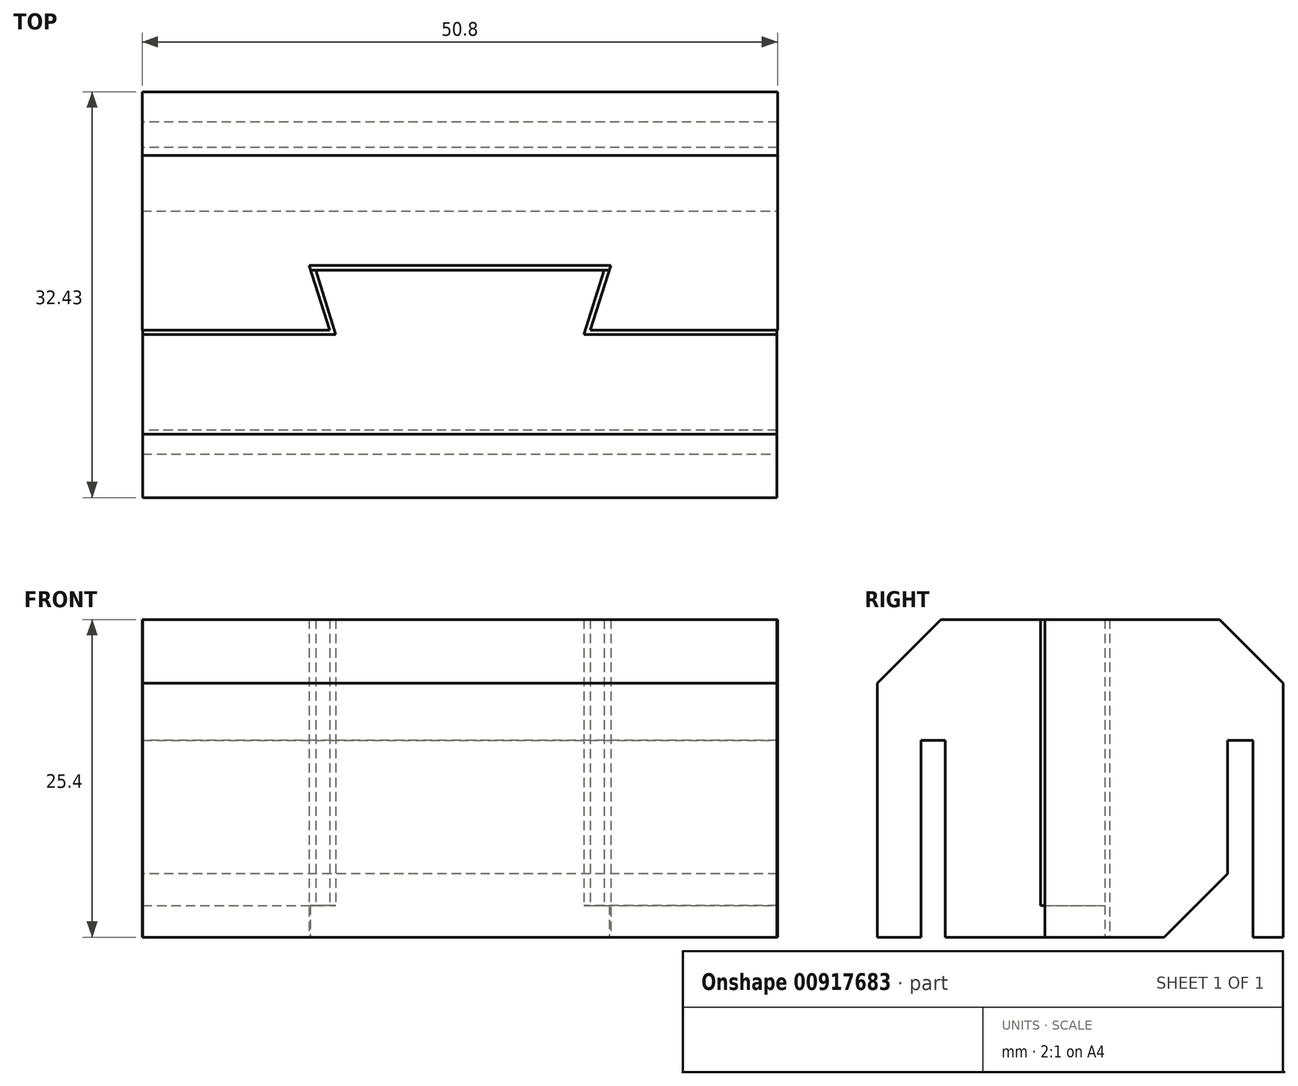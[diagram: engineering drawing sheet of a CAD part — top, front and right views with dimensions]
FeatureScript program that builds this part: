
annotation { "Feature Type Name" : "Feature", "Feature Type Description" : "" }
export const myFeature = defineFeature(function(context is Context, id is Id, definition is map)
    precondition{}
    {
        {
            var Q0;
            Q0=qCreatedBy(makeId("Top.planeOp"),FACE);
            var sketch = newSketch(context, id + "F0", { "sketchPlane" : qUnion([Q0])});
            skLineSegment(sketch, "E0.bottom", {"start": v(25.4, 9.52) * mm, "end": v(-25.4, 9.53) * mm});
            skLineSegment(sketch, "E0.top", {"start": v(25.4, -9.53) * mm, "end": v(10.41, -9.53) * mm});
            skLineSegment(sketch, "E0.left", {"start": v(25.4, 9.52) * mm, "end": v(25.4, -9.53) * mm});
            skLineSegment(sketch, "E0.right", {"start": v(-25.4, 9.53) * mm, "end": v(-25.4, -9.52) * mm});
            skPoint(sketch, "E0.middle", {"position": v(0, 0) * mm});
            skLineSegment(sketch, "E1.bottom", {"start": v(-12.07, -9.53) * mm, "end": v(-10.41, -9.53) * mm});
            skLineSegment(sketch, "E1.top", {"start": v(-12.06, -4.35) * mm, "end": v(12.07, -4.35) * mm});
            skPoint(sketch, "E1.middle", {"position": v(0, -6.94) * mm});
            skLineSegment(sketch, "E2", {"start": v(-12.06, -4.35) * mm, "end": v(-10.41, -9.53) * mm});
            skLineSegment(sketch, "E3.MirrorCS", {"start": v(12.06, -4.35) * mm, "end": v(10.41, -9.52) * mm});
            skLineSegment(sketch, "E4.trimOffspring", {"start": v(-10.41, -9.53) * mm, "end": v(-25.4, -9.53) * mm});
            skLineSegment(sketch, "E5.trimOffspring", {"start": v(10.41, -9.53) * mm, "end": v(12.06, -9.53) * mm});
            skLineSegment(sketch, "E6", {"start": v(-10.41, -9.53) * mm, "end": v(10.41, -9.53) * mm});
            skSolve(sketch);
        }
        {
            var Q0;
            Q0=makeQuery(id+"F0.imprint","IMPRINT",FACE,{"disambiguationData":[TD([[makeQuery(id+"F0.imprint","IMPRINT",EDGE,{"derivedFrom":sQuery(id+"F0.wireOp",EDGE,"E0.bottom")}),1.0]])]});
            extrude(context, id + "F1", {"entities" : qUnion([Q0]), "depth" : 25.4 * mm, "offsetDistance" : 25.4 * mm});
        }
        {
            var Q0;
            Q0=makeQuery(id+"F1.opExtrude","SWEPT_FACE",FACE,{"disambiguationData":[OSD([sQuery(id+"F0.wireOp",EDGE,"E0.right")])]});
            var sketch = newSketch(context, id + "F2", { "sketchPlane" : qUnion([Q0])});
            skLineSegment(sketch, "E7.bottom", {"start": v(-7.13, 0) * mm, "end": v(-5.1, 0) * mm});
            skLineSegment(sketch, "E7.top", {"start": v(-7.13, 15.75) * mm, "end": v(-5.1, 15.75) * mm});
            skLineSegment(sketch, "E7.left", {"start": v(-7.13, 0) * mm, "end": v(-7.13, 15.75) * mm});
            skLineSegment(sketch, "E7.right", {"start": v(-5.1, 0) * mm, "end": v(-5.1, 15.75) * mm});
            skSolve(sketch);
        }
        {
            var Q0;
            Q0=makeQuery(id+"F2.imprint","IMPRINT",FACE,{"disambiguationData":[TD([[makeQuery(id+"F2.imprint","IMPRINT",EDGE,{"derivedFrom":sQuery(id+"F2.wireOp",EDGE,"E7.bottom")}),1.0]])]});
            extrude(context, id + "F3", {"entities" : qUnion([Q0]), "operationType" : NewBodyOperationType.REMOVE, "oppositeDirection" : true, "depth" : 68.33 * mm, "offsetDistance" : 25.4 * mm});
        }
        {
            var Q0;
            Q0=makeQuery(id+"F3.boolean.opBoolean","COPY",EDGE,{"derivedFrom":makeQuery(id+"F3.opExtrude","SWEPT_EDGE",EDGE,{"disambiguationData":[OSD([sQuery(id+"F0.wireOp",EDGE,"E0.right"),sQuery(id+"F2.wireOp",EDGE,"E7.bottom"),sQuery(id+"F2.wireOp",EDGE,"E7.right")])]})});
            var Q1;
            Q1=makeQuery(id+"F1.opExtrude","CAP_EDGE",EDGE,{"disambiguationData":[OSD([sQuery(id+"F0.wireOp",EDGE,"E0.bottom")])],"isStart":false});
            chamfer(context, id + "F4", {"entities" : qUnion([Q0, Q1]), "width" : 5.08 * mm, "tangentPropagation" : true});
        }
        {
            var Q0;
            Q0=qCreatedBy(makeId("Top.planeOp"),FACE);
            var sketch = newSketch(context, id + "F5", { "sketchPlane" : qUnion([Q0])});
            skLineSegment(sketch, "E8", {"start": v(-25.36, -9.86) * mm, "end": v(-9.93, -9.86) * mm});
            skLineSegment(sketch, "E9", {"start": v(-9.93, -9.86) * mm, "end": v(-11.53, -4.72) * mm});
            skLineSegment(sketch, "E10", {"start": v(-11.53, -4.72) * mm, "end": v(0, -4.72) * mm});
            skLineSegment(sketch, "E11", {"start": v(-25.36, -9.86) * mm, "end": v(-25.36, -22.9) * mm});
            skLineSegment(sketch, "E12", {"start": v(-25.36, -22.9) * mm, "end": v(0, -22.9) * mm});
            skLineSegment(sketch, "E13.MirrorCS", {"start": v(25.36, -22.9) * mm, "end": v(0, -22.9) * mm});
            skLineSegment(sketch, "E14.MirrorCS", {"start": v(25.36, -9.86) * mm, "end": v(25.36, -22.9) * mm});
            skLineSegment(sketch, "E15.MirrorCS", {"start": v(25.36, -9.86) * mm, "end": v(9.93, -9.86) * mm});
            skLineSegment(sketch, "E16.MirrorCS", {"start": v(9.93, -9.86) * mm, "end": v(11.53, -4.72) * mm});
            skLineSegment(sketch, "E17.MirrorCS", {"start": v(11.53, -4.72) * mm, "end": v(0, -4.72) * mm});
            skSolve(sketch);
        }
        {
            var Q0;
            Q0=makeQuery(id+"F5.imprint","IMPRINT",FACE,{"disambiguationData":[TD([[makeQuery(id+"F5.imprint","IMPRINT",EDGE,{"derivedFrom":sQuery(id+"F5.wireOp",EDGE,"E8")}),-1.0]])]});
            extrude(context, id + "F6", {"entities" : qUnion([Q0]), "operationType" : NewBodyOperationType.ADD, "depth" : 25.4 * mm, "offsetDistance" : 25.4 * mm});
        }
        {
            var Q0;
            Q0=makeQuery(id+"F6.opExtrude","CAP_FACE",FACE,{"disambiguationData":[OSD([sQuery(id+"F5.wireOp",EDGE,"E8"),sQuery(id+"F5.wireOp",EDGE,"E9"),sQuery(id+"F5.wireOp",EDGE,"E10"),sQuery(id+"F5.wireOp",EDGE,"E11"),sQuery(id+"F5.wireOp",EDGE,"E12"),sQuery(id+"F5.wireOp",EDGE,"E13.MirrorCS"),sQuery(id+"F5.wireOp",EDGE,"E14.MirrorCS"),sQuery(id+"F5.wireOp",EDGE,"E15.MirrorCS"),sQuery(id+"F5.wireOp",EDGE,"E16.MirrorCS"),sQuery(id+"F5.wireOp",EDGE,"E17.MirrorCS")])],"isStart":true});
            var sketch = newSketch(context, id + "F7", { "sketchPlane" : qUnion([Q0])});
            skLineSegment(sketch, "E18", {"start": v(-25.36, 19.4) * mm, "end": v(25.36, 19.4) * mm});
            skLineSegment(sketch, "E19", {"start": v(25.36, 19.4) * mm, "end": v(25.36, 17.5) * mm});
            skLineSegment(sketch, "E20", {"start": v(25.36, 17.5) * mm, "end": v(-25.36, 17.5) * mm});
            skSolve(sketch);
        }
        {
            var Q0;
            {var subQ0=sQuery(id+"F7.wireOp",EDGE,"E18");Q0=makeQuery(id+"F7.imprint","IMPRINT",FACE,{"disambiguationData":[TD([[makeQuery(id+"F7.imprint","IMPRINT",EDGE,{"derivedFrom":subQ0}),-1.0]])]});}
            extrude(context, id + "F8", {"entities" : qUnion([Q0]), "operationType" : NewBodyOperationType.REMOVE, "oppositeDirection" : true, "depth" : 15.75 * mm, "offsetDistance" : 25.4 * mm});
        }
        {
            var Q0;
            {var subQ0=sQuery(id+"F5.wireOp",EDGE,"E17.MirrorCS");var subQ1=sQuery(id+"F5.wireOp",EDGE,"E10");var subQ2=sQuery(id+"F5.wireOp",EDGE,"E9");var subQ3=sQuery(id+"F5.wireOp",EDGE,"E11");var subQ4=sQuery(id+"F5.wireOp",EDGE,"E8");var subQ5=sQuery(id+"F5.wireOp",EDGE,"E14.MirrorCS");var subQ6=sQuery(id+"F5.wireOp",EDGE,"E15.MirrorCS");var subQ7=sQuery(id+"F5.wireOp",EDGE,"E16.MirrorCS");Q0=makeQuery(id+"F8.boolean.opBoolean","SPLIT",FACE,{"disambiguationData":[TD([makeQuery(id+"F6.opExtrude","SWEPT_FACE",FACE,{"disambiguationData":[OSD([subQ4])]})])],"derivedFrom":makeQuery(id+"F6.opExtrude","CAP_FACE",FACE,{"disambiguationData":[OSD([subQ4,subQ2,subQ1,subQ3,sQuery(id+"F5.wireOp",EDGE,"E12"),sQuery(id+"F5.wireOp",EDGE,"E13.MirrorCS"),subQ5,subQ6,subQ7,subQ0])],"isStart":true})});}
            var sketch = newSketch(context, id + "F9", { "sketchPlane" : qUnion([Q0])});
            skLineSegment(sketch, "E21.bottom", {"start": v(-25.36, 9.86) * mm, "end": v(25.36, 9.86) * mm});
            skLineSegment(sketch, "E21.top", {"start": v(-25.36, 4.72) * mm, "end": v(25.36, 4.72) * mm});
            skLineSegment(sketch, "E21.left", {"start": v(-25.36, 9.86) * mm, "end": v(-25.36, 4.72) * mm});
            skLineSegment(sketch, "E21.right", {"start": v(25.36, 9.86) * mm, "end": v(25.36, 4.72) * mm});
            skSolve(sketch);
        }
        {
            var Q0;
            {var subQ0=sQuery(id+"F9.wireOp",EDGE,"E21.left");Q0=makeQuery(id+"F9.imprint","IMPRINT",FACE,{"disambiguationData":[TD([[makeQuery(id+"F9.imprint","IMPRINT",EDGE,{"derivedFrom":subQ0}),1.0]])]});}
            var Q1;
            {var subQ0=sQuery(id+"F9.wireOp",EDGE,"E21.right");Q1=makeQuery(id+"F9.imprint","IMPRINT",FACE,{"disambiguationData":[TD([[makeQuery(id+"F9.imprint","IMPRINT",EDGE,{"derivedFrom":subQ0}),-1.0]])]});}
            extrude(context, id + "F10", {"entities" : qUnion([Q0, Q1]), "operationType" : NewBodyOperationType.ADD, "oppositeDirection" : true, "depth" : 2.54 * mm, "offsetDistance" : 25.4 * mm});
        }
        {
            var Q0;
            Q0=makeQuery(id+"F8.boolean.opBoolean","COPY",EDGE,{"derivedFrom":makeQuery(id+"F8.opExtrude","CAP_EDGE",EDGE,{"disambiguationData":[OSD([sQuery(id+"F7.wireOp",EDGE,"E20")])],"isStart":true})});
            var Q1;
            Q1=makeQuery(id+"F6.opExtrude","CAP_EDGE",EDGE,{"disambiguationData":[OSD([sQuery(id+"F5.wireOp",EDGE,"E12"),sQuery(id+"F5.wireOp",EDGE,"E13.MirrorCS")])],"isStart":false});
            chamfer(context, id + "F11", {"entities" : qUnion([Q0, Q1]), "width" : 5.08 * mm, "tangentPropagation" : true});
        }
    });
